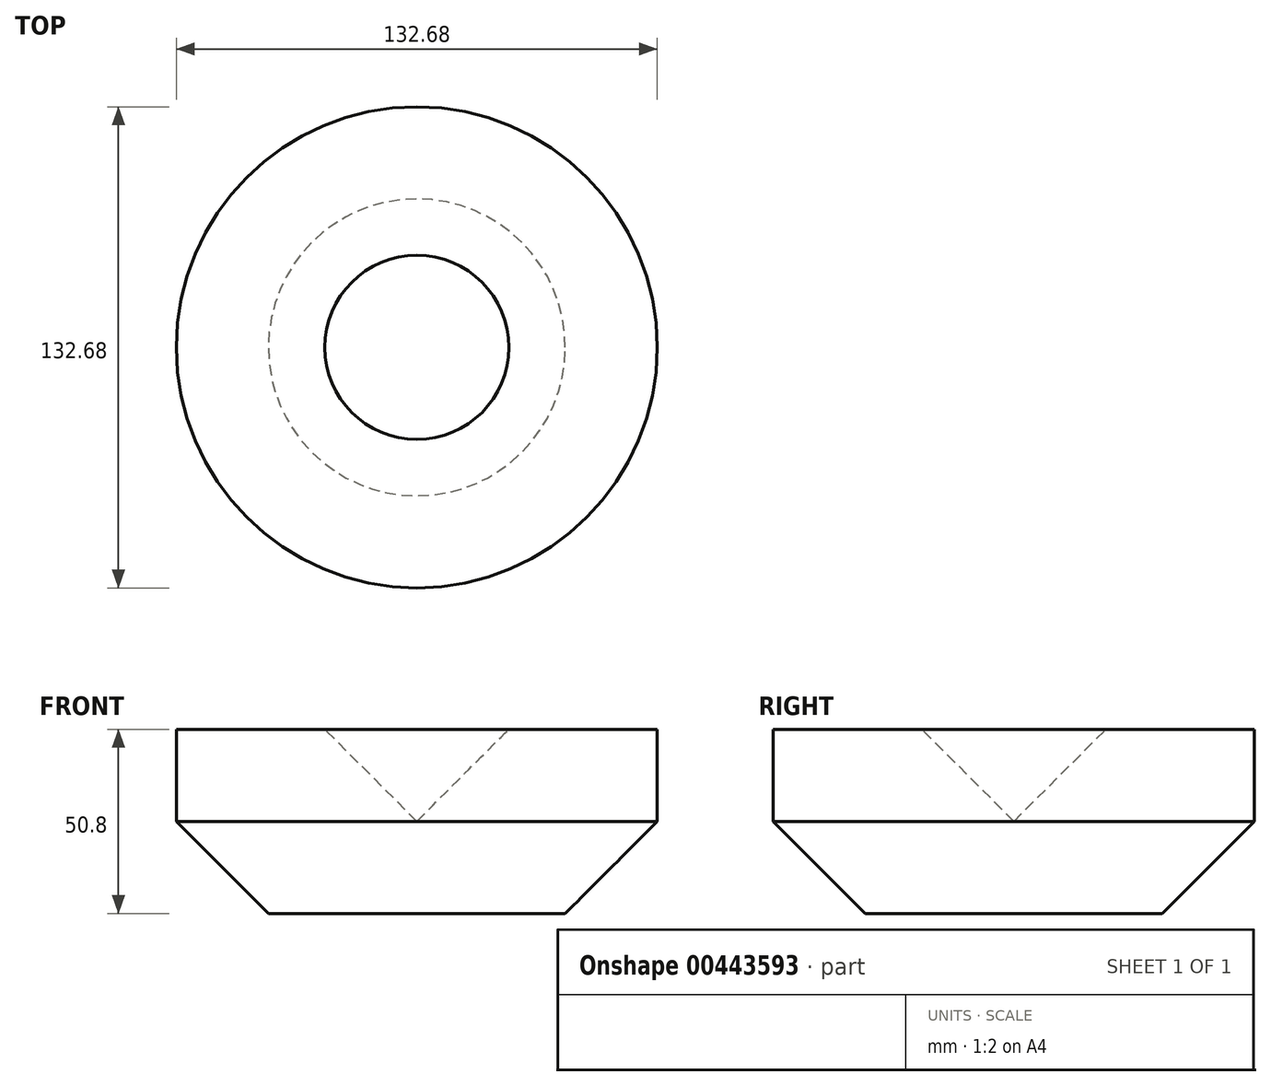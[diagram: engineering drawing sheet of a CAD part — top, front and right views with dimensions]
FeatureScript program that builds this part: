
annotation { "Feature Type Name" : "Feature", "Feature Type Description" : "" }
export const myFeature = defineFeature(function(context is Context, id is Id, definition is map)
    precondition{}
    {
        {
            var Q0;
            Q0=qCreatedBy(makeId("Front.planeOp"),FACE);
            var sketch = newSketch(context, id + "F0", { "sketchPlane" : qUnion([Q0])});
            skLineSegment(sketch, "E0.bottom", {"start": v(-66.34, 25.4) * mm, "end": v(66.34, 25.4) * mm});
            skLineSegment(sketch, "E0.top", {"start": v(-66.34, -25.4) * mm, "end": v(66.34, -25.4) * mm});
            skLineSegment(sketch, "E0.left", {"start": v(-66.34, 25.4) * mm, "end": v(-66.34, -25.4) * mm});
            skLineSegment(sketch, "E0.right", {"start": v(66.34, 25.4) * mm, "end": v(66.34, -25.4) * mm});
            skPoint(sketch, "E0.middle", {"position": v(0, 0) * mm});
            skLineSegment(sketch, "E1", {"start": v(0, 25.4) * mm, "end": v(0, -25.4) * mm});
            skLineSegment(sketch, "E2", {"start": v(-25.4, 25.4) * mm, "end": v(0, 0) * mm});
            skLineSegment(sketch, "E3", {"start": v(0, 0) * mm, "end": v(25.4, 25.4) * mm});
            skLineSegment(sketch, "E4", {"start": v(66.34, 0) * mm, "end": v(40.94, -25.4) * mm});
            skSolve(sketch);
        }
        {
            var Q0;
            {var subQ3=sQuery(id+"F0.wireOp",EDGE,"E3");Q0=makeQuery(id+"F0.imprint","IMPRINT",FACE,{"disambiguationData":[TD([[makeQuery(id+"F0.imprint","IMPRINT",EDGE,{"derivedFrom":subQ3}),-1.0]])]});}
            var Q1;
            Q1=sQuery(id+"F0.wireOp",EDGE,"E1");
            revolve(context, id + "F1", {"entities" : qUnion([Q0]), "axis" : qUnion([Q1]), "revolveType" : RevolveType.FULL});
        }
    });
